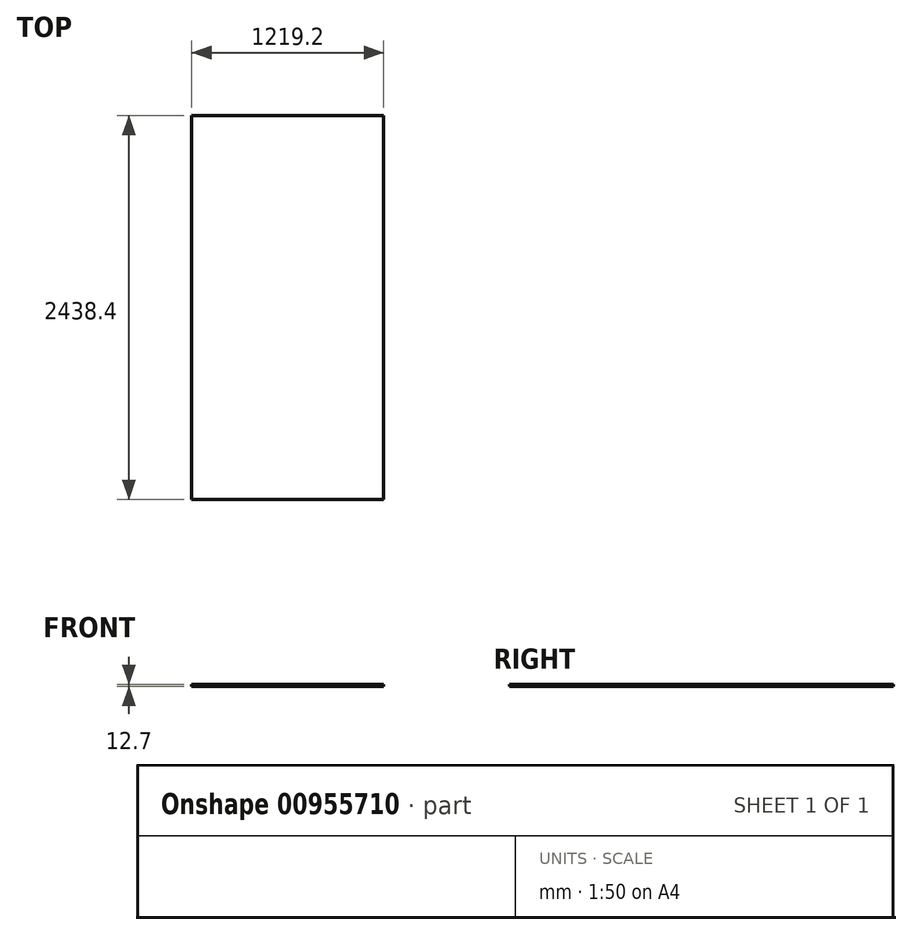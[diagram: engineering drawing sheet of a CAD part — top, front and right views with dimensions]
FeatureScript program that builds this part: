
annotation { "Feature Type Name" : "Feature", "Feature Type Description" : "" }
export const myFeature = defineFeature(function(context is Context, id is Id, definition is map)
    precondition{}
    {
        {
            var Q0;
            Q0=qCreatedBy(makeId("Top.planeOp"),FACE);
            var sketch = newSketch(context, id + "F0", { "sketchPlane" : qUnion([Q0])});
            skLineSegment(sketch, "E0.bottom", {"start": v(609.6, -1219.2) * mm, "end": v(-609.6, -1219.2) * mm});
            skLineSegment(sketch, "E0.top", {"start": v(609.6, 1219.2) * mm, "end": v(-609.6, 1219.2) * mm});
            skLineSegment(sketch, "E0.left", {"start": v(609.6, -1219.2) * mm, "end": v(609.6, 1219.2) * mm});
            skLineSegment(sketch, "E0.right", {"start": v(-609.6, -1219.2) * mm, "end": v(-609.6, 1219.2) * mm});
            skPoint(sketch, "E0.middle", {"position": v(0, 0) * mm});
            skSolve(sketch);
        }
        {
            var Q0;
            Q0 = qSketchRegion(id + "F0", true);
            extrude(context, id + "F1", {"entities" : qUnion([Q0]), "depth" : 12.7 * mm, "offsetDistance" : 25.4 * mm});
        }
    });
